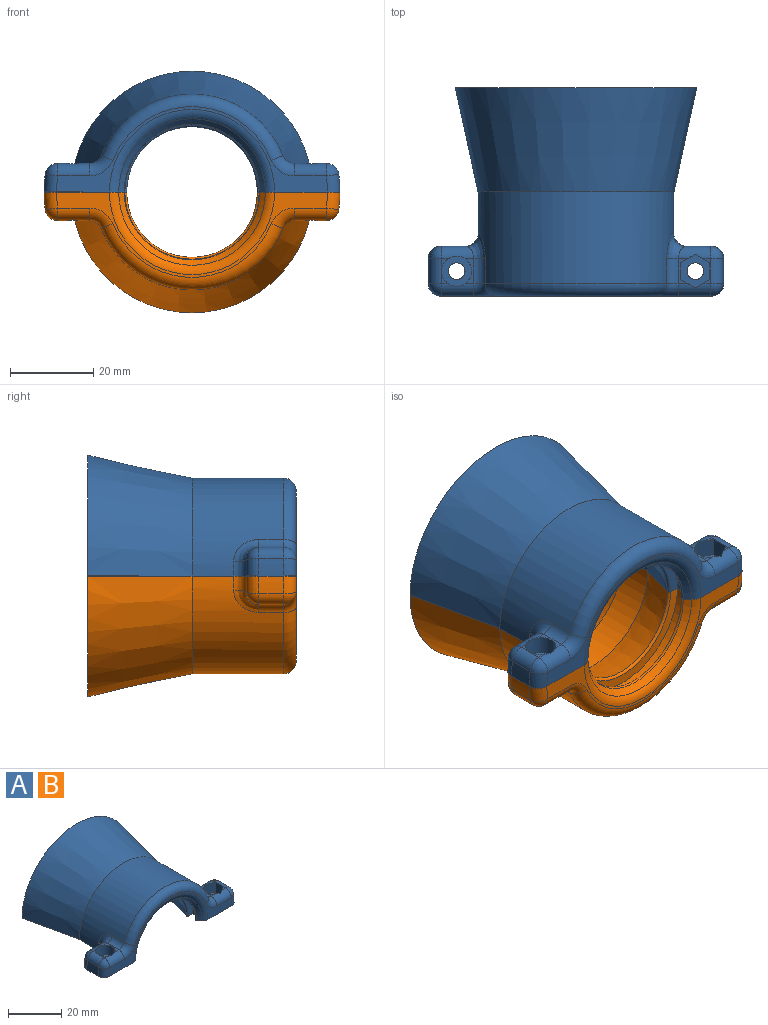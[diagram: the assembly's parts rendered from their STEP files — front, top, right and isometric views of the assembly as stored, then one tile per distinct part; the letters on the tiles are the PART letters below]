
ASSEMBLY  parts=2 mates=1
PART A: 59 faces, bbox 71.2x50x29 mm
  f0: plane 6x1.81mm, normal (0,0,1), area 2.4mm2, adj f9,f13,f14,f38,f39,f44
  f1: plane 2.77x1.58mm, normal (0,0,1), area 1.4mm2, adj f33,f51,f57
  f2: plane 2.77x1.58mm, normal (0,0,1), area 1.4mm2, adj f33,f48,f51
  f3: plane 6x2.25mm, normal (0,0,1), area 5mm2, adj f10,f11,f12,f38,f43,f44
  f4: plane 6.28x3.87mm, normal (0,1,0), area 23.3mm2, adj f7,f35,f37,f38
  f5: plane 65x20.5mm, normal (0,-1,0), area 142.8mm2, adj f7,f26,f40,f44,f45,f46,f47,f48
  f6: cylinder r=35.5mm len=6mm, axis (0,1,0), area 25.4mm2, adj f7,f35,f39,f40
  f7: plane 50x19.83mm, normal (0,0,-1), area 398.8mm2, adj f4,f5,f6,f8,f16,f17,f18,f19
  f8: cylinder r=2mm len=4mm, axis (0,0,1), area 29.8mm2, adj f7,f15
  f9: plane 4.53x3.53mm, normal (-0.5,-0.87,0), area 18.1mm2, adj f0,f10,f14,f15,f38
  f10: plane 4.53x3.53mm, normal (0.5,-0.87,0), area 18.1mm2, adj f3,f9,f11,f15,f38
  f11: plane 4.5x4.04mm, normal (1,0,0), area 18.2mm2, adj f3,f10,f12,f15
  f12: plane 4.53x3.53mm, normal (0.5,0.87,0), area 18.1mm2, adj f3,f11,f13,f15,f44
  f13: plane 4.53x3.53mm, normal (-0.5,0.87,0), area 18.1mm2, adj f0,f12,f14,f15,f44
  f14: plane 4.5x4.04mm, normal (-1,0,0), area 18.2mm2, adj f0,f9,f13,f15
  f15: plane 8.08x7mm, normal (0,0,1), area 29.9mm2, adj f8,f9,f10,f11,f12,f13,f14
  f16: cylinder r=23.5mm len=47mm, axis (0,1,0), area 1423.4mm2, adj f7,f17,f26,f37,f41,f43,f47,f53
  f17: cone r=23.5mm half-angle=12.4deg, axis (0,1,0), area 2111mm2, adj f7,f16,f18,f26
  f18: plane 58x29mm, normal (0,1,0), area 416.3mm2, adj f7,f17,f19,f26
  f19: cone r=18.5mm half-angle=12.4deg, axis (0,1,0), area 1708.9mm2, adj f7,f18,f20,f26
  f20: cylinder r=18.5mm len=37mm, axis (0,1,0), area 482.4mm2, adj f7,f19,f21,f26
  f21: cone r=15.5mm half-angle=16.7deg, axis (0,1,0), area 524.7mm2, adj f7,f20,f26,f27
  f22: plane 37x18.5mm, normal (0,-1,0), area 126.8mm2, adj f7,f23,f26,f27
  f23: cylinder r=18.5mm len=37mm, axis (0,1,0), area 197.6mm2, adj f7,f22,f24,f26
  f24: plane 37x18.5mm, normal (0,1,0), area 103.2mm2, adj f7,f23,f26,f28
  f25: cone r=15.5mm half-angle=42.3deg, axis (0,-1,0), area 106.5mm2, adj f7,f26,f28,f58
  f26: plane 50x19.83mm, normal (0,0,-1), area 398.8mm2, adj f5,f16,f17,f18,f19,f20,f21,f22
  f27: torus R=16.17mm, axis (0,-1,0), area 46.3mm2, adj f7,f21,f22,f26
  f28: torus R=16.63mm, axis (0,-1,0), area 59mm2, adj f7,f24,f25,f26
  f29: cylinder r=35.5mm len=6mm, axis (0,1,0), area 25.4mm2, adj f26,f46,f51,f52
  f30: plane 6.28x3.87mm, normal (0,1,0), area 23.3mm2, adj f26,f52,f53,f57
  f31: plane 6x2.02mm, normal (0,0,1), area 5.4mm2, adj f33,f48,f54,f57
  f32: cylinder r=2mm len=4mm, axis (0,0,1), area 29.8mm2, adj f26,f34
  f33: cylinder r=3.62mm len=7.25mm, axis (0,0,1), area 102.5mm2, adj f1,f2,f31,f34,f48,f51,f57
  f34: plane 7.25x7.25mm, normal (0,0,1), area 28.7mm2, adj f32,f33
  f35: torus R=32.5mm, axis (0,1,0), area 19.4mm2, adj f4,f6,f7,f36
  f36: sphere r=3mm, area 13.3mm2, adj f35,f38,f39
  f37: torus R=26.5mm, axis (0,1,0), area 17mm2, adj f4,f7,f16,f41
  f38: cylinder r=3mm len=7.68mm, axis (1,0,0), area 31mm2, adj f0,f3,f4,f9,f10,f36,f41
  f39: cylinder r=3mm len=6mm, axis (0,1,0), area 26.1mm2, adj f0,f6,f36,f42
  f40: torus R=32.5mm, axis (0,1,0), area 19.4mm2, adj f5,f6,f7,f42
  f41: bspline ~7.26x6.08mm, area 26.3mm2, adj f16,f37,f38,f43
  f42: sphere r=3mm, area 13.1mm2, adj f39,f40,f44
  f43: cylinder r=3mm len=6mm, axis (0,1,0), area 21.4mm2, adj f3,f16,f41,f45
  f44: cylinder r=3mm len=7.68mm, axis (1,0,0), area 34.3mm2, adj f0,f3,f5,f12,f13,f42,f45
  f45: torus R=6mm, axis (0,1,0), area 22.9mm2, adj f5,f43,f44,f47
  f46: torus R=32.5mm, axis (0,1,0), area 19.4mm2, adj f5,f26,f29,f49
  f47: torus R=20.5mm, axis (0,1,0), area 251.2mm2, adj f5,f16,f45,f50
  f48: cylinder r=3mm len=7.68mm, axis (1,0,0), area 34.4mm2, adj f2,f5,f31,f33,f49,f50
  f49: sphere r=3mm, area 13.3mm2, adj f46,f48,f51
  f50: torus R=6mm, axis (0,1,0), area 22.9mm2, adj f5,f47,f48,f54
  f51: cylinder r=3mm len=6mm, axis (0,1,0), area 26.1mm2, adj f1,f2,f29,f33,f49,f55
  f52: torus R=32.5mm, axis (0,1,0), area 19.4mm2, adj f26,f29,f30,f55
  f53: torus R=26.5mm, axis (0,1,0), area 17mm2, adj f16,f26,f30,f56
  f54: cylinder r=3mm len=6mm, axis (0,1,0), area 21.4mm2, adj f16,f31,f50,f56
  f55: sphere r=3mm, area 13.3mm2, adj f51,f52,f57
  f56: bspline ~7.08x6.49mm, area 26.3mm2, adj f16,f53,f54,f57
  f57: cylinder r=3mm len=7.68mm, axis (1,0,0), area 31.2mm2, adj f1,f30,f31,f33,f55,f56
  f58: torus R=19.83mm, axis (0,1,0), area 146.4mm2, adj f5,f7,f25,f26
PART B: same geometry as A
PLACE A at identity fixed
PLACE B rot(axis=(0,1,0),180deg) t=(0,0,0)mm
MATE cylindrical A.f26 <-> B.f7  axis (0,0,1) through (-16.63,-16.4,0)mm
